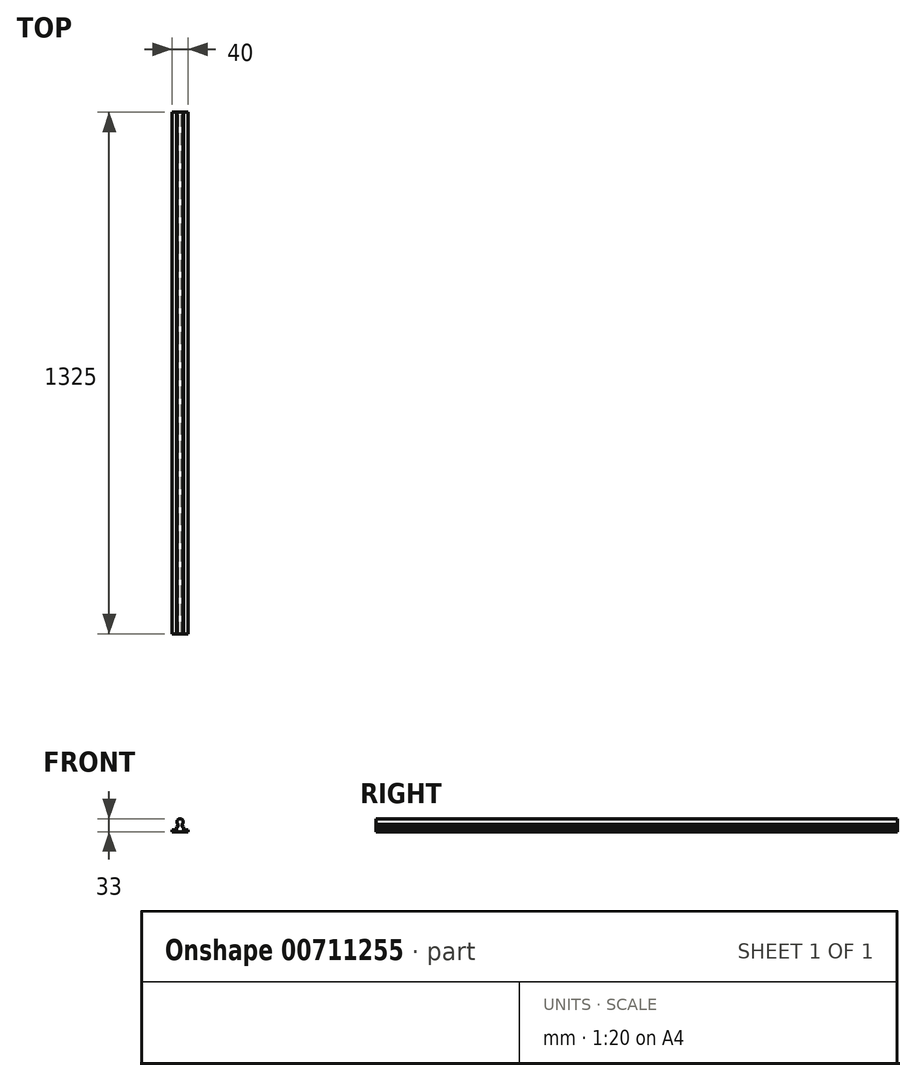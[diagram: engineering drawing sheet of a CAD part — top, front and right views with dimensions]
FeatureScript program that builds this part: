
annotation { "Feature Type Name" : "Feature", "Feature Type Description" : "" }
export const myFeature = defineFeature(function(context is Context, id is Id, definition is map)
    precondition{}
    {
        {
            var Q0;
            Q0=qCreatedBy(makeId("Front.planeOp"),FACE);
            var sketch = newSketch(context, id + "F0", { "sketchPlane" : qUnion([Q0])});
            skLineSegment(sketch, "E0.top", {"start": v(20, -2.5) * mm, "end": v(-20, -2.5) * mm});
            skLineSegment(sketch, "E0.left", {"start": v(20, 2.5) * mm, "end": v(20, -2.5) * mm});
            skLineSegment(sketch, "E0.right", {"start": v(-20, 2.5) * mm, "end": v(-20, -2.5) * mm});
            skPoint(sketch, "E0.middle", {"position": v(0, 0) * mm});
            skArc(sketch, "E1", {"start": v(4, 15.57) * mm, "mid": v(0, 30.5) * mm, "end": v(-4, 15.57) * mm});
            skLineSegment(sketch, "E2", {"start": v(-20, 2.5) * mm, "end": v(-8.9, 2.5) * mm});
            skLineSegment(sketch, "E3", {"start": v(20, 2.5) * mm, "end": v(8.9, 2.5) * mm});
            skLineSegment(sketch, "E4", {"start": v(-8.9, 2.5) * mm, "end": v(-8.9, 9.2) * mm});
            skLineSegment(sketch, "E5", {"start": v(8.9, 2.5) * mm, "end": v(8.9, 9.2) * mm});
            skLineSegment(sketch, "E6", {"start": v(-8.9, 9.2) * mm, "end": v(-7.68, 9.2) * mm});
            skLineSegment(sketch, "E7", {"start": v(8.9, 9.2) * mm, "end": v(7.68, 9.2) * mm});
            skLineSegment(sketch, "E8", {"start": v(-7.68, 9.2) * mm, "end": v(-4, 15.57) * mm});
            skLineSegment(sketch, "E9", {"start": v(7.68, 9.2) * mm, "end": v(4, 15.57) * mm});
            skLineSegment(sketch, "E10.trimOffspring", {"start": v(-8.9, 2.5) * mm, "end": v(-20, 2.5) * mm});
            skSolve(sketch);
        }
        {
            var Q0;
            Q0=makeQuery(id+"F0.imprint","IMPRINT",FACE,{"disambiguationData":[TD([[makeQuery(id+"F0.imprint","IMPRINT",EDGE,{"derivedFrom":sQuery(id+"F0.wireOp",EDGE,"E0.top")}),-1.0]])]});
            extrude(context, id + "F1", {"entities" : qUnion([Q0]), "endBound" : BoundingType.SYMMETRIC, "depth" : 1325 * mm, "offsetDistance" : 25 * mm});
        }
    });
